# Revit family: Accesories-Teknion-CQCMT-Routes-Utility_cart-R2022
name_source: partatom
category: Furniture
units: mm (PartAtom-declared; Revit-internal decimal feet)

## family parameters
Always vertical = Yes
Cut with Voids When Loaded = No
OmniClass Number = 23.40.20.00
OmniClass Title = General Furniture and Specialties
Render Appearance Source = Family Geometry
Room Calculation Point = No
Shared = Yes
Work Plane-Based = No

## types (1)
- CQCMT42P
    Assembly Code = E2020200
    Back Panel Finish = Fabric-Teknion-L109-Preforated_Black
    Default Elevation = 0 "
    Depth = 0 "
    Description = Utility Cart - Routes
    Height = 63 "
    Length = 0 "
    Manufacturer = Teknion
    Manufacturer Fax = 416.661.4586
    Model = CQCMT42P
    Part Number = CQCMT
    Product Documentation Link = https://assets.teknion.com
    Product Line = Utility Cart
    Product Page URL = https://www.teknion.com
    Series = Routes
    Sustainability Data = https://www.teknion.com
    URL = www.teknion.com
    Unit Weight URL = http://www.teknion.com
    Warranty = http://www.teknion.com
    Width = 0 "

## geometry (parser evidence)
native form markers: Sweep x4
no freeform markers — native parametric forms only
